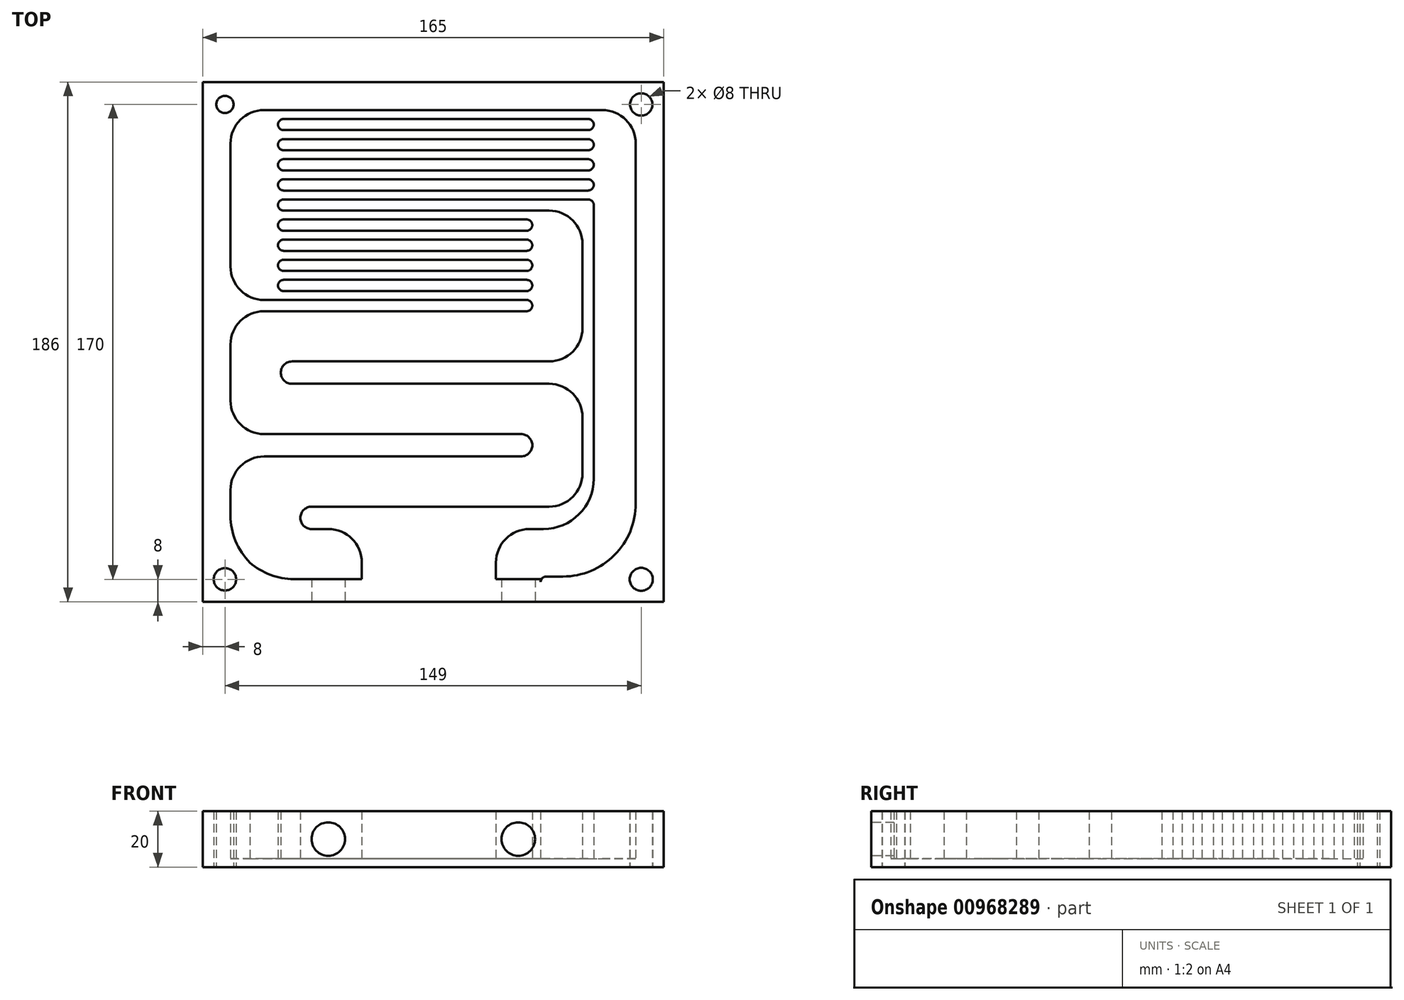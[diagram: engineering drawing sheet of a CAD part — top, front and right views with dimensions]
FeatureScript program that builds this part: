
annotation { "Feature Type Name" : "Feature", "Feature Type Description" : "" }
export const myFeature = defineFeature(function(context is Context, id is Id, definition is map)
    precondition{}
    {
        {
            var Q0;
            Q0=qCreatedBy(makeId("Top.planeOp"),FACE);
            var sketch = newSketch(context, id + "F0", { "sketchPlane" : qUnion([Q0])});
            skLineSegment(sketch, "E0.bottom", {"start": v(-82.5, -93) * mm, "end": v(82.5, -93) * mm});
            skLineSegment(sketch, "E0.top", {"start": v(-82.5, 93) * mm, "end": v(82.5, 93) * mm});
            skLineSegment(sketch, "E0.left", {"start": v(-82.5, -93) * mm, "end": v(-82.5, 93) * mm});
            skLineSegment(sketch, "E0.right", {"start": v(82.5, -93) * mm, "end": v(82.5, 93) * mm});
            skPoint(sketch, "E0.middle", {"position": v(0, 0) * mm});
            skLineSegment(sketch, "E1.bottom", {"start": v(34.5, -67) * mm, "end": v(39.5, -67) * mm});
            skLineSegment(sketch, "E1.top", {"start": v(40.5, -84) * mm, "end": v(46.5, -84) * mm});
            skLineSegment(sketch, "E1.left", {"start": v(22.5, -79) * mm, "end": v(22.5, -84) * mm});
            skLineSegment(sketch, "E2.top", {"start": v(60.5, 83) * mm, "end": v(57.5, 83) * mm});
            skLineSegment(sketch, "E2.left", {"start": v(72.5, -57.9) * mm, "end": v(72.5, 71) * mm});
            skLineSegment(sketch, "E2.right", {"start": v(57.5, -49) * mm, "end": v(57.5, 49) * mm});
            skLineSegment(sketch, "E3.bottom", {"start": v(57.5, 83) * mm, "end": v(-60.5, 83) * mm});
            skLineSegment(sketch, "E3.top", {"start": v(55.5, 79.8) * mm, "end": v(-53.5, 79.8) * mm});
            skLineSegment(sketch, "E4.bottom", {"start": v(-60.5, 83) * mm, "end": v(-55.5, 83) * mm});
            skLineSegment(sketch, "E4.top", {"start": v(-60.5, 15) * mm, "end": v(-55.5, 15) * mm});
            skLineSegment(sketch, "E4.left", {"start": v(-72.5, 71) * mm, "end": v(-72.5, 27) * mm});
            skLineSegment(sketch, "E4.right", {"start": v(-55.5, 77.8) * mm, "end": v(-55.5, 77.8) * mm});
            skLineSegment(sketch, "E5.bottom", {"start": v(55.5, 75.8) * mm, "end": v(-53.5, 75.8) * mm});
            skLineSegment(sketch, "E5.top", {"start": v(55.5, 72.6) * mm, "end": v(-53.5, 72.6) * mm});
            skLineSegment(sketch, "E6.bottom", {"start": v(-53.5, 68.6) * mm, "end": v(55.5, 68.6) * mm});
            skLineSegment(sketch, "E6.top", {"start": v(-53.5, 65.4) * mm, "end": v(55.5, 65.4) * mm});
            skLineSegment(sketch, "E7.bottom", {"start": v(-53.5, 61.4) * mm, "end": v(55.5, 61.4) * mm});
            skLineSegment(sketch, "E7.top", {"start": v(-53.5, 58.2) * mm, "end": v(55.5, 58.2) * mm});
            skLineSegment(sketch, "E8.bottom", {"start": v(-53.5, 54.2) * mm, "end": v(55.5, 54.2) * mm});
            skLineSegment(sketch, "E8.top", {"start": v(-53.5, 51) * mm, "end": v(55.5, 51) * mm});
            skLineSegment(sketch, "E9.trimOffspring", {"start": v(57.5, 77.8) * mm, "end": v(57.5, 77.8) * mm});
            skLineSegment(sketch, "E10.trimOffspring", {"start": v(57.5, 70.6) * mm, "end": v(57.5, 70.6) * mm});
            skLineSegment(sketch, "E11.trimOffspring", {"start": v(57.5, 63.4) * mm, "end": v(57.5, 63.4) * mm});
            skLineSegment(sketch, "E12.trimOffspring", {"start": v(57.5, 56.2) * mm, "end": v(57.5, 56.2) * mm});
            skPoint(sketch, "E13.visualSharp", {"position": v(57.5, 79.8) * mm});
            skArc(sketch, "E13.filletArc", {"start": v(57.5, 77.8) * mm, "mid": v(56.91, 79.21) * mm, "end": v(55.5, 79.8) * mm});
            skPoint(sketch, "E14.visualSharp", {"position": v(57.5, 75.8) * mm});
            skArc(sketch, "E14.filletArc", {"start": v(55.5, 75.8) * mm, "mid": v(56.91, 76.39) * mm, "end": v(57.5, 77.8) * mm});
            skPoint(sketch, "E15.visualSharp", {"position": v(57.5, 72.6) * mm});
            skArc(sketch, "E15.filletArc", {"start": v(57.5, 70.6) * mm, "mid": v(56.91, 72.01) * mm, "end": v(55.5, 72.6) * mm});
            skPoint(sketch, "E16.visualSharp", {"position": v(57.5, 68.6) * mm});
            skArc(sketch, "E16.filletArc", {"start": v(55.5, 68.6) * mm, "mid": v(56.91, 69.19) * mm, "end": v(57.5, 70.6) * mm});
            skPoint(sketch, "E17.visualSharp", {"position": v(57.5, 61.4) * mm});
            skArc(sketch, "E17.filletArc", {"start": v(55.5, 61.4) * mm, "mid": v(56.91, 61.99) * mm, "end": v(57.5, 63.4) * mm});
            skPoint(sketch, "E18.visualSharp", {"position": v(57.5, 65.4) * mm});
            skArc(sketch, "E18.filletArc", {"start": v(57.5, 63.4) * mm, "mid": v(56.91, 64.81) * mm, "end": v(55.5, 65.4) * mm});
            skPoint(sketch, "E19.visualSharp", {"position": v(57.5, 58.2) * mm});
            skArc(sketch, "E19.filletArc", {"start": v(57.5, 56.2) * mm, "mid": v(56.91, 57.61) * mm, "end": v(55.5, 58.2) * mm});
            skPoint(sketch, "E20.visualSharp", {"position": v(57.5, 54.2) * mm});
            skArc(sketch, "E20.filletArc", {"start": v(55.5, 54.2) * mm, "mid": v(56.91, 54.79) * mm, "end": v(57.5, 56.2) * mm});
            skPoint(sketch, "E21.visualSharp", {"position": v(72.5, 83) * mm});
            skArc(sketch, "E21.filletArc", {"start": v(72.5, 71) * mm, "mid": v(68.99, 79.49) * mm, "end": v(60.5, 83) * mm});
            skPoint(sketch, "E22.visualSharp", {"position": v(57.5, 51) * mm});
            skArc(sketch, "E22.filletArc", {"start": v(57.5, 49) * mm, "mid": v(56.91, 50.41) * mm, "end": v(55.5, 51) * mm});
            skLineSegment(sketch, "E23.trimOffspring", {"start": v(-55.5, 70.6) * mm, "end": v(-55.5, 70.6) * mm});
            skLineSegment(sketch, "E24.trimOffspring", {"start": v(-55.5, 63.4) * mm, "end": v(-55.5, 63.4) * mm});
            skLineSegment(sketch, "E25.trimOffspring", {"start": v(-55.5, 56.2) * mm, "end": v(-55.5, 56.2) * mm});
            skLineSegment(sketch, "E26.trimOffspring", {"start": v(-55.5, 49) * mm, "end": v(-55.5, 49) * mm});
            skPoint(sketch, "E27.visualSharp", {"position": v(-55.5, 79.8) * mm});
            skArc(sketch, "E27.filletArc", {"start": v(-53.5, 79.8) * mm, "mid": v(-54.91, 79.21) * mm, "end": v(-55.5, 77.8) * mm});
            skPoint(sketch, "E28.visualSharp", {"position": v(-55.5, 72.6) * mm});
            skArc(sketch, "E28.filletArc", {"start": v(-53.5, 72.6) * mm, "mid": v(-54.91, 72.01) * mm, "end": v(-55.5, 70.6) * mm});
            skPoint(sketch, "E29.visualSharp", {"position": v(-55.5, 65.4) * mm});
            skArc(sketch, "E29.filletArc", {"start": v(-53.5, 65.4) * mm, "mid": v(-54.91, 64.81) * mm, "end": v(-55.5, 63.4) * mm});
            skPoint(sketch, "E30.visualSharp", {"position": v(-55.5, 58.2) * mm});
            skArc(sketch, "E30.filletArc", {"start": v(-53.5, 58.2) * mm, "mid": v(-54.91, 57.61) * mm, "end": v(-55.5, 56.2) * mm});
            skPoint(sketch, "E31.visualSharp", {"position": v(-55.5, 51) * mm});
            skArc(sketch, "E31.filletArc", {"start": v(-53.5, 51) * mm, "mid": v(-54.91, 50.41) * mm, "end": v(-55.5, 49) * mm});
            skPoint(sketch, "E32.visualSharp", {"position": v(-55.5, 75.8) * mm});
            skArc(sketch, "E32.filletArc", {"start": v(-55.5, 77.8) * mm, "mid": v(-54.91, 76.39) * mm, "end": v(-53.5, 75.8) * mm});
            skPoint(sketch, "E33.visualSharp", {"position": v(-55.5, 68.6) * mm});
            skArc(sketch, "E33.filletArc", {"start": v(-55.5, 70.6) * mm, "mid": v(-54.91, 69.19) * mm, "end": v(-53.5, 68.6) * mm});
            skPoint(sketch, "E34.visualSharp", {"position": v(-55.5, 61.4) * mm});
            skArc(sketch, "E34.filletArc", {"start": v(-55.5, 63.4) * mm, "mid": v(-54.91, 61.99) * mm, "end": v(-53.5, 61.4) * mm});
            skPoint(sketch, "E35.visualSharp", {"position": v(-55.5, 54.2) * mm});
            skArc(sketch, "E35.filletArc", {"start": v(-55.5, 56.2) * mm, "mid": v(-54.91, 54.79) * mm, "end": v(-53.5, 54.2) * mm});
            skPoint(sketch, "E36.visualSharp", {"position": v(-72.5, 83) * mm});
            skArc(sketch, "E36.filletArc", {"start": v(-60.5, 83) * mm, "mid": v(-68.99, 79.49) * mm, "end": v(-72.5, 71) * mm});
            skLineSegment(sketch, "E37.bottom", {"start": v(35.5, 47) * mm, "end": v(41.5, 47) * mm});
            skLineSegment(sketch, "E37.top", {"start": v(40.5, -7) * mm, "end": v(41.5, -7) * mm});
            skLineSegment(sketch, "E37.left", {"start": v(35.5, 41.8) * mm, "end": v(35.5, 41.8) * mm});
            skLineSegment(sketch, "E37.right", {"start": v(53.5, 35) * mm, "end": v(53.5, 5) * mm});
            skLineSegment(sketch, "E38.bottom", {"start": v(35.5, 47) * mm, "end": v(-53.5, 47) * mm});
            skLineSegment(sketch, "E38.top", {"start": v(33.5, 43.8) * mm, "end": v(-53.5, 43.8) * mm});
            skLineSegment(sketch, "E39.bottom", {"start": v(-53.5, 39.8) * mm, "end": v(33.5, 39.8) * mm});
            skLineSegment(sketch, "E39.top", {"start": v(-53.5, 36.6) * mm, "end": v(33.5, 36.6) * mm});
            skLineSegment(sketch, "E40.bottom", {"start": v(-53.5, 32.6) * mm, "end": v(33.5, 32.6) * mm});
            skLineSegment(sketch, "E40.top", {"start": v(-53.5, 29.4) * mm, "end": v(33.5, 29.4) * mm});
            skLineSegment(sketch, "E41.bottom", {"start": v(-53.5, 25.4) * mm, "end": v(33.5, 25.4) * mm});
            skLineSegment(sketch, "E41.top", {"start": v(-53.5, 22.2) * mm, "end": v(33.5, 22.2) * mm});
            skLineSegment(sketch, "E42.bottom", {"start": v(-53.5, 18.2) * mm, "end": v(33.5, 18.2) * mm});
            skLineSegment(sketch, "E42.top", {"start": v(-55.5, 15) * mm, "end": v(33.5, 15) * mm});
            skLineSegment(sketch, "E43.trimOffspring", {"start": v(-55.5, 41.8) * mm, "end": v(-55.5, 41.8) * mm});
            skLineSegment(sketch, "E44.trimOffspring", {"start": v(-55.5, 34.6) * mm, "end": v(-55.5, 34.6) * mm});
            skLineSegment(sketch, "E45.trimOffspring", {"start": v(-55.5, 27.4) * mm, "end": v(-55.5, 27.4) * mm});
            skLineSegment(sketch, "E46.trimOffspring", {"start": v(-55.5, 20.2) * mm, "end": v(-55.5, 20.2) * mm});
            skPoint(sketch, "E47.visualSharp", {"position": v(-55.5, 47) * mm});
            skArc(sketch, "E47.filletArc", {"start": v(-55.5, 49) * mm, "mid": v(-54.91, 47.59) * mm, "end": v(-53.5, 47) * mm});
            skPoint(sketch, "E48.visualSharp", {"position": v(-55.5, 43.8) * mm});
            skArc(sketch, "E48.filletArc", {"start": v(-53.5, 43.8) * mm, "mid": v(-54.91, 43.21) * mm, "end": v(-55.5, 41.8) * mm});
            skPoint(sketch, "E49.visualSharp", {"position": v(-55.5, 39.8) * mm});
            skArc(sketch, "E49.filletArc", {"start": v(-55.5, 41.8) * mm, "mid": v(-54.91, 40.39) * mm, "end": v(-53.5, 39.8) * mm});
            skPoint(sketch, "E50.visualSharp", {"position": v(-55.5, 36.6) * mm});
            skArc(sketch, "E50.filletArc", {"start": v(-53.5, 36.6) * mm, "mid": v(-54.91, 36.01) * mm, "end": v(-55.5, 34.6) * mm});
            skPoint(sketch, "E51.visualSharp", {"position": v(-55.5, 29.4) * mm});
            skArc(sketch, "E51.filletArc", {"start": v(-53.5, 29.4) * mm, "mid": v(-54.91, 28.81) * mm, "end": v(-55.5, 27.4) * mm});
            skPoint(sketch, "E52.visualSharp", {"position": v(-55.5, 32.6) * mm});
            skArc(sketch, "E52.filletArc", {"start": v(-55.5, 34.6) * mm, "mid": v(-54.91, 33.19) * mm, "end": v(-53.5, 32.6) * mm});
            skPoint(sketch, "E53.visualSharp", {"position": v(-55.5, 25.4) * mm});
            skArc(sketch, "E53.filletArc", {"start": v(-55.5, 27.4) * mm, "mid": v(-54.91, 25.99) * mm, "end": v(-53.5, 25.4) * mm});
            skPoint(sketch, "E54.visualSharp", {"position": v(-55.5, 22.2) * mm});
            skArc(sketch, "E54.filletArc", {"start": v(-53.5, 22.2) * mm, "mid": v(-54.91, 21.61) * mm, "end": v(-55.5, 20.2) * mm});
            skPoint(sketch, "E55.visualSharp", {"position": v(-55.5, 18.2) * mm});
            skArc(sketch, "E55.filletArc", {"start": v(-55.5, 20.2) * mm, "mid": v(-54.91, 18.79) * mm, "end": v(-53.5, 18.2) * mm});
            skLineSegment(sketch, "E56.trimOffspring", {"start": v(35.5, 34.6) * mm, "end": v(35.5, 34.6) * mm});
            skLineSegment(sketch, "E57.trimOffspring", {"start": v(35.5, 27.4) * mm, "end": v(35.5, 27.4) * mm});
            skLineSegment(sketch, "E58.trimOffspring", {"start": v(35.5, 20.2) * mm, "end": v(35.5, 20.2) * mm});
            skLineSegment(sketch, "E59.trimOffspring", {"start": v(35.5, 13) * mm, "end": v(35.5, 13) * mm});
            skPoint(sketch, "E60.visualSharp", {"position": v(35.5, 43.8) * mm});
            skArc(sketch, "E60.filletArc", {"start": v(35.5, 41.8) * mm, "mid": v(34.91, 43.21) * mm, "end": v(33.5, 43.8) * mm});
            skPoint(sketch, "E61.visualSharp", {"position": v(35.5, 36.6) * mm});
            skArc(sketch, "E61.filletArc", {"start": v(35.5, 34.6) * mm, "mid": v(34.91, 36.01) * mm, "end": v(33.5, 36.6) * mm});
            skPoint(sketch, "E62.visualSharp", {"position": v(35.5, 29.4) * mm});
            skArc(sketch, "E62.filletArc", {"start": v(35.5, 27.4) * mm, "mid": v(34.91, 28.81) * mm, "end": v(33.5, 29.4) * mm});
            skPoint(sketch, "E63.visualSharp", {"position": v(35.5, 22.2) * mm});
            skArc(sketch, "E63.filletArc", {"start": v(35.5, 20.2) * mm, "mid": v(34.91, 21.61) * mm, "end": v(33.5, 22.2) * mm});
            skPoint(sketch, "E64.visualSharp", {"position": v(35.5, 39.8) * mm});
            skArc(sketch, "E64.filletArc", {"start": v(33.5, 39.8) * mm, "mid": v(34.91, 40.39) * mm, "end": v(35.5, 41.8) * mm});
            skPoint(sketch, "E65.visualSharp", {"position": v(35.5, 32.6) * mm});
            skArc(sketch, "E65.filletArc", {"start": v(33.5, 32.6) * mm, "mid": v(34.91, 33.19) * mm, "end": v(35.5, 34.6) * mm});
            skPoint(sketch, "E66.visualSharp", {"position": v(35.5, 25.4) * mm});
            skArc(sketch, "E66.filletArc", {"start": v(33.5, 25.4) * mm, "mid": v(34.91, 25.99) * mm, "end": v(35.5, 27.4) * mm});
            skPoint(sketch, "E67.visualSharp", {"position": v(35.5, 18.2) * mm});
            skArc(sketch, "E67.filletArc", {"start": v(33.5, 18.2) * mm, "mid": v(34.91, 18.79) * mm, "end": v(35.5, 20.2) * mm});
            skPoint(sketch, "E68.visualSharp", {"position": v(35.5, 15) * mm});
            skArc(sketch, "E68.filletArc", {"start": v(35.5, 13) * mm, "mid": v(34.91, 14.41) * mm, "end": v(33.5, 15) * mm});
            skPoint(sketch, "E69.visualSharp", {"position": v(-72.5, 15) * mm});
            skArc(sketch, "E69.filletArc", {"start": v(-72.5, 27) * mm, "mid": v(-68.99, 18.51) * mm, "end": v(-60.5, 15) * mm});
            skPoint(sketch, "E70.visualSharp", {"position": v(53.5, 47) * mm});
            skArc(sketch, "E70.filletArc", {"start": v(53.5, 35) * mm, "mid": v(49.99, 43.49) * mm, "end": v(41.5, 47) * mm});
            skLineSegment(sketch, "E71.bottom", {"start": v(33.5, 11) * mm, "end": v(-54.5, 11) * mm});
            skLineSegment(sketch, "E71.top", {"start": v(40.5, -7) * mm, "end": v(-50.5, -7) * mm});
            skLineSegment(sketch, "E72.bottom", {"start": v(-54.5, 11) * mm, "end": v(-60.5, 11) * mm});
            skLineSegment(sketch, "E72.top", {"start": v(-54.5, -33) * mm, "end": v(-60.5, -33) * mm});
            skLineSegment(sketch, "E72.left", {"start": v(-54.5, -11) * mm, "end": v(-54.5, -11) * mm});
            skLineSegment(sketch, "E72.right", {"start": v(-72.5, -1) * mm, "end": v(-72.5, -21) * mm});
            skLineSegment(sketch, "E73.bottom", {"start": v(-54.5, -33) * mm, "end": v(31.5, -33) * mm});
            skLineSegment(sketch, "E73.top", {"start": v(-50.5, -15) * mm, "end": v(35.5, -15) * mm});
            skLineSegment(sketch, "E74.bottom", {"start": v(35.5, -15) * mm, "end": v(41.5, -15) * mm});
            skLineSegment(sketch, "E74.top", {"start": v(35.5, -59) * mm, "end": v(41.5, -59) * mm});
            skLineSegment(sketch, "E74.left", {"start": v(35.5, -37) * mm, "end": v(35.5, -37) * mm});
            skLineSegment(sketch, "E74.right", {"start": v(53.5, -27) * mm, "end": v(53.5, -47) * mm});
            skLineSegment(sketch, "E75.bottom", {"start": v(35.5, -59) * mm, "end": v(-43.5, -59) * mm});
            skLineSegment(sketch, "E75.top", {"start": v(31.5, -41) * mm, "end": v(-54.5, -41) * mm});
            skLineSegment(sketch, "E76.bottom", {"start": v(-54.5, -41) * mm, "end": v(-60.5, -41) * mm});
            skLineSegment(sketch, "E76.right", {"start": v(-72.5, -53) * mm, "end": v(-72.5, -62.15) * mm});
            skPoint(sketch, "E77.visualSharp", {"position": v(53.5, -7) * mm});
            skArc(sketch, "E77.filletArc", {"start": v(41.5, -7) * mm, "mid": v(49.99, -3.49) * mm, "end": v(53.5, 5) * mm});
            skPoint(sketch, "E78.visualSharp", {"position": v(-72.5, 11) * mm});
            skArc(sketch, "E78.filletArc", {"start": v(-60.5, 11) * mm, "mid": v(-68.99, 7.49) * mm, "end": v(-72.5, -1) * mm});
            skPoint(sketch, "E79.visualSharp", {"position": v(-72.5, -33) * mm});
            skArc(sketch, "E79.filletArc", {"start": v(-72.5, -21) * mm, "mid": v(-68.99, -29.49) * mm, "end": v(-60.5, -33) * mm});
            skPoint(sketch, "E80.visualSharp", {"position": v(53.5, -15) * mm});
            skArc(sketch, "E80.filletArc", {"start": v(53.5, -27) * mm, "mid": v(49.99, -18.51) * mm, "end": v(41.5, -15) * mm});
            skPoint(sketch, "E81.visualSharp", {"position": v(53.5, -59) * mm});
            skArc(sketch, "E81.filletArc", {"start": v(41.5, -59) * mm, "mid": v(49.99, -55.49) * mm, "end": v(53.5, -47) * mm});
            skPoint(sketch, "E82.visualSharp", {"position": v(-72.5, -41) * mm});
            skArc(sketch, "E82.filletArc", {"start": v(-60.5, -41) * mm, "mid": v(-68.99, -44.51) * mm, "end": v(-72.5, -53) * mm});
            skPoint(sketch, "E83.visualSharp", {"position": v(-54.5, -7) * mm});
            skArc(sketch, "E83.filletArc", {"start": v(-50.5, -7) * mm, "mid": v(-53.33, -8.17) * mm, "end": v(-54.5, -11) * mm});
            skPoint(sketch, "E84.visualSharp", {"position": v(-54.5, -15) * mm});
            skArc(sketch, "E84.filletArc", {"start": v(-54.5, -11) * mm, "mid": v(-53.33, -13.83) * mm, "end": v(-50.5, -15) * mm});
            skPoint(sketch, "E85.visualSharp", {"position": v(35.5, -33) * mm});
            skArc(sketch, "E85.filletArc", {"start": v(35.5, -37) * mm, "mid": v(34.33, -34.17) * mm, "end": v(31.5, -33) * mm});
            skPoint(sketch, "E86.visualSharp", {"position": v(35.5, -41) * mm});
            skArc(sketch, "E86.filletArc", {"start": v(31.5, -41) * mm, "mid": v(34.33, -39.83) * mm, "end": v(35.5, -37) * mm});
            skPoint(sketch, "E87.visualSharp", {"position": v(57.5, -67) * mm});
            skArc(sketch, "E87.filletArc", {"start": v(39.5, -67) * mm, "mid": v(52.23, -61.73) * mm, "end": v(57.5, -49) * mm});
            skLineSegment(sketch, "E88.bottom", {"start": v(-49.83, -84.9) * mm, "end": v(-25.5, -84.9) * mm});
            skLineSegment(sketch, "E88.top", {"start": v(-43.5, -67) * mm, "end": v(-37.5, -67) * mm});
            skLineSegment(sketch, "E88.right", {"start": v(-25.5, -84.9) * mm, "end": v(-25.5, -79) * mm});
            skCircle(sketch, "E89", {"center": v(74.5, -85) * mm, "radius": 4.12 * mm});
            skLineSegment(sketch, "E90", {"start": v(-47.5, -63) * mm, "end": v(-47.5, -63) * mm});
            skArc(sketch, "E91.filletArc", {"start": v(-72.5, -62.15) * mm, "mid": v(-70.7, -71.27) * mm, "end": v(-65.56, -79.03) * mm});
            skPoint(sketch, "E92.visualSharp", {"position": v(-59.31, -84.9) * mm});
            skArc(sketch, "E92.filletArc", {"start": v(-65.56, -79.03) * mm, "mid": v(-58.22, -83.38) * mm, "end": v(-49.83, -84.9) * mm});
            skPoint(sketch, "E76.top.end.orphan", {"position": v(-72.5, -84.9) * mm});
            skPoint(sketch, "E93.visualSharp", {"position": v(72.5, -84) * mm});
            skArc(sketch, "E93.filletArc", {"start": v(46.5, -84) * mm, "mid": v(64.92, -76.35) * mm, "end": v(72.5, -57.9) * mm});
            skLineSegment(sketch, "E94.top", {"start": v(22.5, -84.9) * mm, "end": v(38.5, -84.9) * mm});
            skLineSegment(sketch, "E94.left", {"start": v(22.5, -84) * mm, "end": v(22.5, -84.9) * mm});
            skLineSegment(sketch, "E94.right", {"start": v(38.5, -84.9) * mm, "end": v(38.5, -86) * mm});
            skPoint(sketch, "E95.visualSharp", {"position": v(22.5, -67) * mm});
            skArc(sketch, "E95.filletArc", {"start": v(34.5, -67) * mm, "mid": v(26.01, -70.51) * mm, "end": v(22.5, -79) * mm});
            skPoint(sketch, "E96.visualSharp", {"position": v(38.5, -84) * mm});
            skArc(sketch, "E96.filletArc", {"start": v(40.5, -84) * mm, "mid": v(39.09, -84.59) * mm, "end": v(38.5, -86) * mm});
            skPoint(sketch, "E97.visualSharp", {"position": v(-25.5, -67) * mm});
            skArc(sketch, "E97.filletArc", {"start": v(-25.5, -79) * mm, "mid": v(-29.01, -70.51) * mm, "end": v(-37.5, -67) * mm});
            skPoint(sketch, "E98.visualSharp", {"position": v(-47.5, -59) * mm});
            skArc(sketch, "E98.filletArc", {"start": v(-43.5, -59) * mm, "mid": v(-46.33, -60.17) * mm, "end": v(-47.5, -63) * mm});
            skPoint(sketch, "E99.visualSharp", {"position": v(-47.5, -67) * mm});
            skArc(sketch, "E99.filletArc", {"start": v(-47.5, -63) * mm, "mid": v(-46.33, -65.83) * mm, "end": v(-43.5, -67) * mm});
            skPoint(sketch, "E100.visualSharp", {"position": v(35.5, 11) * mm});
            skArc(sketch, "E100.filletArc", {"start": v(33.5, 11) * mm, "mid": v(34.91, 11.59) * mm, "end": v(35.5, 13) * mm});
            skCircle(sketch, "E101", {"center": v(-74.5, -85) * mm, "radius": 4 * mm});
            skCircle(sketch, "E102", {"center": v(74.5, 85) * mm, "radius": 4 * mm});
            skCircle(sketch, "E103", {"center": v(-74.5, 85) * mm, "radius": 3.07 * mm});
            skPoint(sketch, "E104.orphan", {"position": v(35.5, -7) * mm});
            skSolve(sketch);
        }
        {
            var Q0;
            Q0 = qSketchRegion(id + "F0", true);
            var Q1;
            Q1=makeQuery(id+"F0.imprint","IMPRINT",FACE,{"disambiguationData":[TD([[makeQuery(id+"F0.imprint","IMPRINT",EDGE,{"derivedFrom":sQuery(id+"F0.wireOp",EDGE,"E1.bottom")}),-1.0]])]});
            var Q2;
            Q2=makeQuery(id+"F0.imprint","IMPRINT",FACE,{"disambiguationData":[TD([[makeQuery(id+"F0.imprint","IMPRINT",EDGE,{"derivedFrom":sQuery(id+"F0.wireOp",EDGE,"E7.top")}),-1.0]])]});
            var Q3;
            Q3=makeQuery(id+"F0.imprint","IMPRINT",FACE,{"disambiguationData":[TD([[makeQuery(id+"F0.imprint","IMPRINT",EDGE,{"derivedFrom":sQuery(id+"F0.wireOp",EDGE,"E6.top")}),-1.0]])]});
            var Q4;
            Q4=makeQuery(id+"F0.imprint","IMPRINT",FACE,{"disambiguationData":[TD([[makeQuery(id+"F0.imprint","IMPRINT",EDGE,{"derivedFrom":sQuery(id+"F0.wireOp",EDGE,"E5.top")}),1.0]])]});
            var Q5;
            Q5=makeQuery(id+"F0.imprint","IMPRINT",FACE,{"disambiguationData":[TD([[makeQuery(id+"F0.imprint","IMPRINT",EDGE,{"derivedFrom":sQuery(id+"F0.wireOp",EDGE,"E3.top")}),1.0]])]});
            var Q6;
            Q6=makeQuery(id+"F0.imprint","IMPRINT",FACE,{"disambiguationData":[TD([[makeQuery(id+"F0.imprint","IMPRINT",EDGE,{"derivedFrom":sQuery(id+"F0.wireOp",EDGE,"E38.top")}),1.0]])]});
            var Q7;
            Q7=makeQuery(id+"F0.imprint","IMPRINT",FACE,{"disambiguationData":[TD([[makeQuery(id+"F0.imprint","IMPRINT",EDGE,{"derivedFrom":sQuery(id+"F0.wireOp",EDGE,"E39.top")}),-1.0]])]});
            var Q8;
            Q8=makeQuery(id+"F0.imprint","IMPRINT",FACE,{"disambiguationData":[TD([[makeQuery(id+"F0.imprint","IMPRINT",EDGE,{"derivedFrom":sQuery(id+"F0.wireOp",EDGE,"E40.top")}),-1.0]])]});
            var Q9;
            Q9=makeQuery(id+"F0.imprint","IMPRINT",FACE,{"disambiguationData":[TD([[makeQuery(id+"F0.imprint","IMPRINT",EDGE,{"derivedFrom":sQuery(id+"F0.wireOp",EDGE,"E41.top")}),-1.0]])]});
            extrude(context, id + "F1", {"entities" : qUnion([Q0, Q1, Q2, Q3, Q4, Q5, Q6, Q7, Q8, Q9]), "depth" : 3 * mm, "offsetDistance" : 25 * mm});
        }
        {
            var Q0;
            Q0=makeQuery(id+"F0.imprint","IMPRINT",FACE,{"disambiguationData":[TD([[makeQuery(id+"F0.imprint","IMPRINT",EDGE,{"derivedFrom":sQuery(id+"F0.wireOp",EDGE,"E0.bottom")}),1.0]])]});
            var Q1;
            Q1=makeQuery(id+"F0.imprint","IMPRINT",FACE,{"disambiguationData":[TD([[makeQuery(id+"F0.imprint","IMPRINT",EDGE,{"derivedFrom":sQuery(id+"F0.wireOp",EDGE,"E3.top")}),1.0]])]});
            var Q2;
            Q2=makeQuery(id+"F0.imprint","IMPRINT",FACE,{"disambiguationData":[TD([[makeQuery(id+"F0.imprint","IMPRINT",EDGE,{"derivedFrom":sQuery(id+"F0.wireOp",EDGE,"E5.top")}),1.0]])]});
            var Q3;
            Q3=makeQuery(id+"F0.imprint","IMPRINT",FACE,{"disambiguationData":[TD([[makeQuery(id+"F0.imprint","IMPRINT",EDGE,{"derivedFrom":sQuery(id+"F0.wireOp",EDGE,"E6.top")}),-1.0]])]});
            var Q4;
            Q4=makeQuery(id+"F0.imprint","IMPRINT",FACE,{"disambiguationData":[TD([[makeQuery(id+"F0.imprint","IMPRINT",EDGE,{"derivedFrom":sQuery(id+"F0.wireOp",EDGE,"E7.top")}),-1.0]])]});
            var Q5;
            Q5=makeQuery(id+"F0.imprint","IMPRINT",FACE,{"disambiguationData":[TD([[makeQuery(id+"F0.imprint","IMPRINT",EDGE,{"derivedFrom":sQuery(id+"F0.wireOp",EDGE,"E38.top")}),1.0]])]});
            var Q6;
            Q6=makeQuery(id+"F0.imprint","IMPRINT",FACE,{"disambiguationData":[TD([[makeQuery(id+"F0.imprint","IMPRINT",EDGE,{"derivedFrom":sQuery(id+"F0.wireOp",EDGE,"E39.top")}),-1.0]])]});
            var Q7;
            Q7=makeQuery(id+"F0.imprint","IMPRINT",FACE,{"disambiguationData":[TD([[makeQuery(id+"F0.imprint","IMPRINT",EDGE,{"derivedFrom":sQuery(id+"F0.wireOp",EDGE,"E40.top")}),-1.0]])]});
            var Q8;
            Q8=makeQuery(id+"F0.imprint","IMPRINT",FACE,{"disambiguationData":[TD([[makeQuery(id+"F0.imprint","IMPRINT",EDGE,{"derivedFrom":sQuery(id+"F0.wireOp",EDGE,"E41.top")}),-1.0]])]});
            extrude(context, id + "F2", {"entities" : qUnion([Q0, Q1, Q2, Q3, Q4, Q5, Q6, Q7, Q8]), "operationType" : NewBodyOperationType.ADD, "depth" : 20 * mm, "offsetDistance" : 25 * mm});
        }
        {
            var Q0;
            {var subQ0=sQuery(id+"F0.wireOp",EDGE,"E0.bottom");Q0=makeQuery(id+"F2.boolean.opBoolean","MERGE",FACE,{"derivedFrom":[makeQuery(id+"F1.opExtrude","SWEPT_FACE",FACE,{"disambiguationData":[OSD([subQ0])]}),makeQuery(id+"F2.opExtrude","SWEPT_FACE",FACE,{"disambiguationData":[OSD([subQ0])]})]});}
            var sketch = newSketch(context, id + "F3", { "sketchPlane" : qUnion([Q0])});
            skCircle(sketch, "E105", {"center": v(-37.5, 10) * mm, "radius": 6 * mm});
            skCircle(sketch, "E106", {"center": v(30.5, 10) * mm, "radius": 6 * mm});
            skSolve(sketch);
        }
        {
            var Q0;
            Q0 = qSketchRegion(id + "F3", true);
            extrude(context, id + "F4", {"entities" : qUnion([Q0]), "operationType" : NewBodyOperationType.REMOVE, "endBound" : BoundingType.UP_TO_NEXT, "oppositeDirection" : true, "depth" : 25 * mm, "offsetDistance" : 25 * mm});
        }
    });
